# Revit family: Gira_202800
name_source: partatom
category: Allgemeines Modell
revit_build: Autodesk Revit 2017 (Build: 20160225_1515(x64)
units: mm (PartAtom-declared; Revit-internal decimal feet)

## family parameters
Basisbauteil = Fläche
Beim Laden mit Abzugskörper schneiden = Nein
Bemaßung runder Anschluss = Durchmesser verwenden
Gemeinsam genutzt = Nein
Kann Basisbauteil für Bewehrung sein = Nein
Raumberechnungspunkt = Nein
Teiletyp = Normal

## types (1)
- Gira_202800
    App control via Bluetooth = Nein
    Applicable with button = Ja
    Applicable with infrared button = Nein
    Applicable with movement sensor = Nein
    Applicable with presence indicator = Nein
    Applicable with time switch/timer = Nein
    Applicable with transmission button = Nein
    Assembly arrangement = Basic element
    BIM = https://media.stage.bim.site
    Beschreibung = DALI poti PSU Ins.,DALI potentiometer with integrated power supply unit,,,Features:,- For switching on off and adjusting brightness for lights with a DALI interface,- Integrated power supply according to DALI specification (DIN IEC 60926) for 26 DALI devices.,- Parallel connection of up to 4 DALI potentiometers with integrated power supply unit to supply up to 104 DALI devices.,- Can be operated simultaneously from several operating points. Communication is via Broadcast.,- A basic brightness or a switch-on brightness can be stored.,,Notes :,- When selecting the DALI power supply, the number of DALI devices and the DALI potentiometer (always counts as 1 device) must be considered.
    Colour = Other
    Connection type = Screwed terminal
    Data sheet = https://katalog.gira.de
    Dimming phase cut-off = Nein
    Dimming phase cut-on = Nein
    Frequency [Hz] = [50:60]
    GTIN = 4010337023456
    HAN = 202800
    Halogen free = Nein
    Hersteller = Gira
    Light value memory = Nein
    Material = Other
    Material quality = Other
    Method of operation = Turn/push button
    Mounting method = Flush mounted (plaster)
    Nominal voltage [Volt] 1 = [230:230]
    Productwebsite = http://katalog.gira.de
    Serial dimmer = Nein
    Substation input = Nein
    Suitable for degree of protection (IP) = IP20
    Surface protection = Other
    Transparent = Nein
    Type of fastening = Mounting with screw
    Type of load = Other
    Typname = DALI potentiom. pow.supply unit Insert
    URL = https://www.gira.de
    Vorgabe-Ansicht = 1219 mm

## geometry (parser evidence)
native form markers: Sweep x2
no freeform markers — native parametric forms only
